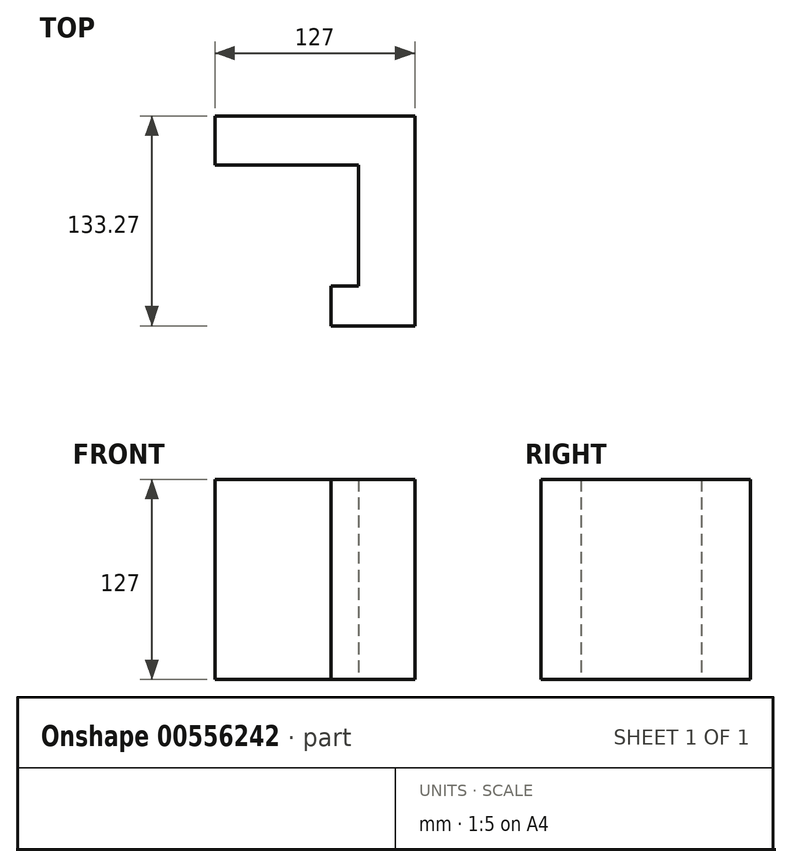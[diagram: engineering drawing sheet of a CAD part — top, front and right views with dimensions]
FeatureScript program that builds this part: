
annotation { "Feature Type Name" : "Feature", "Feature Type Description" : "" }
export const myFeature = defineFeature(function(context is Context, id is Id, definition is map)
    precondition{}
    {
        {
            var Q0;
            Q0=qCreatedBy(makeId("Top.planeOp"),FACE);
            var sketch = newSketch(context, id + "F0", { "sketchPlane" : qUnion([Q0])});
            skLineSegment(sketch, "E0.bottom", {"start": v(-30.35, 62.57) * mm, "end": v(5.27, 62.57) * mm});
            skLineSegment(sketch, "E0.top", {"start": v(-30.35, -14.23) * mm, "end": v(5.27, -14.23) * mm});
            skLineSegment(sketch, "E0.left", {"start": v(-30.35, 62.57) * mm, "end": v(-30.35, -14.23) * mm});
            skLineSegment(sketch, "E0.right", {"start": v(5.27, 62.57) * mm, "end": v(5.27, -14.23) * mm});
            skLineSegment(sketch, "E1.bottom", {"start": v(5.27, 62.57) * mm, "end": v(-121.73, 62.57) * mm});
            skLineSegment(sketch, "E1.top", {"start": v(5.27, 93.64) * mm, "end": v(-121.73, 93.64) * mm});
            skLineSegment(sketch, "E1.left", {"start": v(5.27, 62.57) * mm, "end": v(5.27, 93.64) * mm});
            skLineSegment(sketch, "E1.right", {"start": v(-121.73, 62.57) * mm, "end": v(-121.73, 93.64) * mm});
            skLineSegment(sketch, "E2.bottom", {"start": v(-121.73, 62.57) * mm, "end": v(-83.63, 62.57) * mm});
            skLineSegment(sketch, "E2.top", {"start": v(-121.73, -58.76) * mm, "end": v(-83.63, -58.76) * mm});
            skLineSegment(sketch, "E2.left", {"start": v(-121.73, 62.57) * mm, "end": v(-121.73, -58.76) * mm});
            skLineSegment(sketch, "E2.right", {"start": v(-83.63, 62.57) * mm, "end": v(-83.63, -58.76) * mm});
            skLineSegment(sketch, "E3.bottom", {"start": v(5.27, -14.23) * mm, "end": v(-48.07, -14.23) * mm});
            skLineSegment(sketch, "E3.top", {"start": v(5.27, -39.63) * mm, "end": v(-48.07, -39.63) * mm});
            skLineSegment(sketch, "E3.left", {"start": v(5.27, -14.23) * mm, "end": v(5.27, -39.63) * mm});
            skLineSegment(sketch, "E3.right", {"start": v(-48.07, -14.23) * mm, "end": v(-48.07, -39.63) * mm});
            skSolve(sketch);
        }
        {
            var Q0;
            Q0=makeQuery(id+"F0.imprint","IMPRINT",FACE,{"disambiguationData":[TD([[makeQuery(id+"F0.imprint","IMPRINT",EDGE,{"derivedFrom":sQuery(id+"F0.wireOp",EDGE,"E2.bottom")}),-1.0]])]});
            var Q1;
            Q1=makeQuery(id+"F0.imprint","IMPRINT",FACE,{"disambiguationData":[TD([[makeQuery(id+"F0.imprint","IMPRINT",EDGE,{"derivedFrom":sQuery(id+"F0.wireOp",EDGE,"E1.top")}),1.0]])]});
            var Q2;
            {var subQ0=sQuery(id+"F0.wireOp",EDGE,"E0.left");Q2=makeQuery(id+"F0.imprint","IMPRINT",FACE,{"disambiguationData":[TD([[makeQuery(id+"F0.imprint","IMPRINT",EDGE,{"derivedFrom":subQ0}),1.0]])]});}
            var Q3;
            Q3=makeQuery(id+"F0.imprint","IMPRINT",FACE,{"disambiguationData":[TD([[makeQuery(id+"F0.imprint","IMPRINT",EDGE,{"derivedFrom":sQuery(id+"F0.wireOp",EDGE,"E3.top")}),-1.0]])]});
            extrude(context, id + "F1", {"entities" : qUnion([Q0, Q1, Q2, Q3]), "depth" : 127 * mm, "offsetDistance" : 25.4 * mm});
        }
    });
